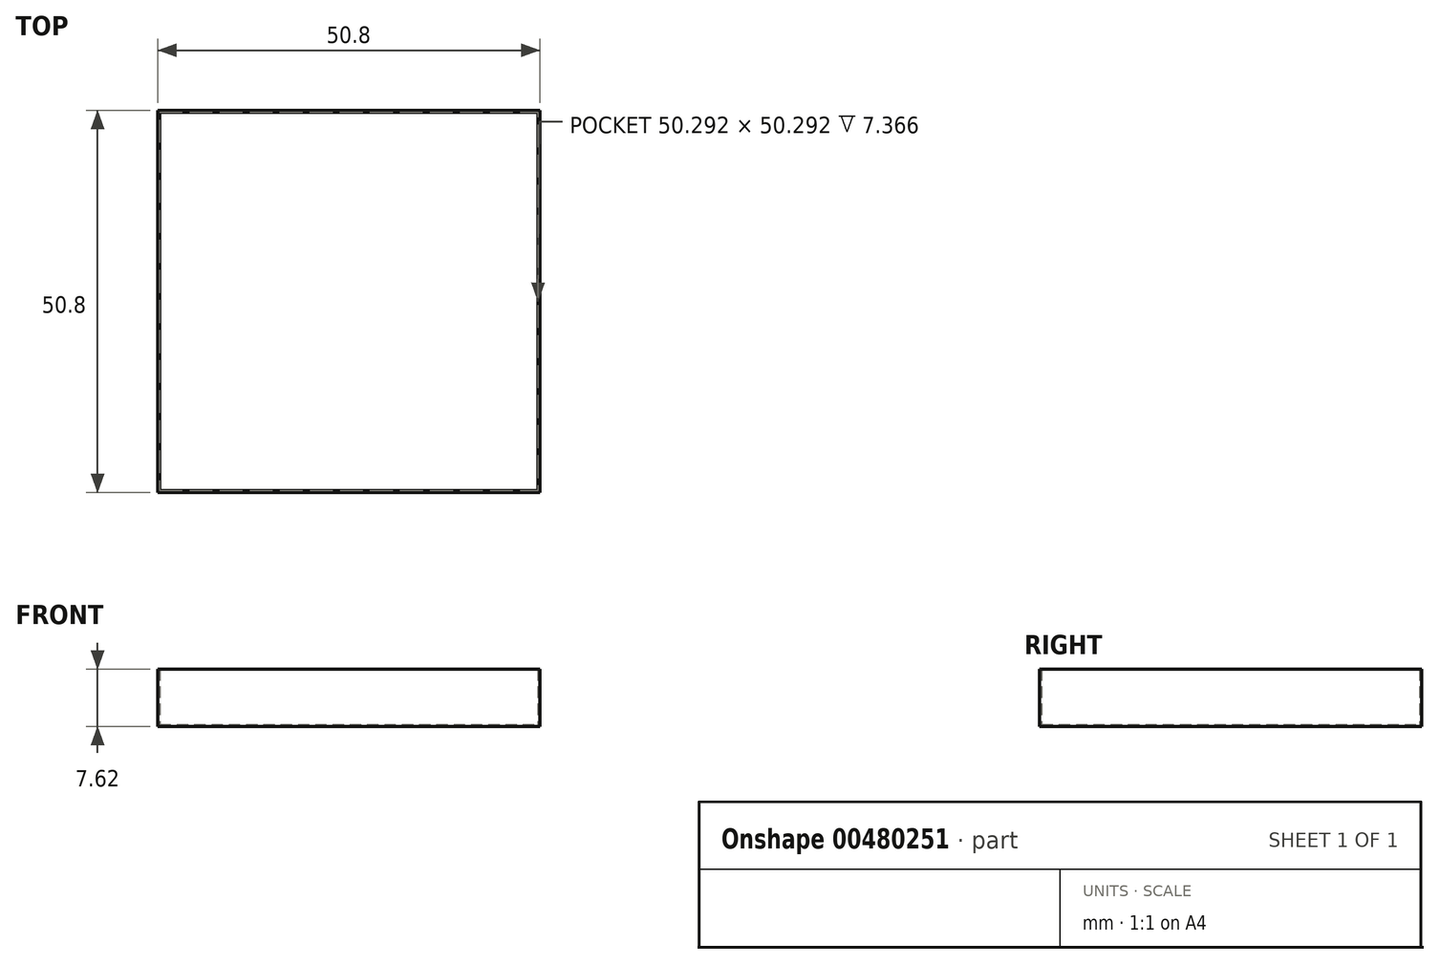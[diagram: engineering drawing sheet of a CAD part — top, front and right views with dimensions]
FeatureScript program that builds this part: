
annotation { "Feature Type Name" : "Feature", "Feature Type Description" : "" }
export const myFeature = defineFeature(function(context is Context, id is Id, definition is map)
    precondition{}
    {
        {
            var Q0;
            Q0=qCreatedBy(makeId("Top.planeOp"),FACE);
            var sketch = newSketch(context, id + "F0", { "sketchPlane" : qUnion([Q0])});
            skPoint(sketch, "E0.middle", {"position": v(0, 0) * mm});
            skPoint(sketch, "E0.right.start.orphan", {"position": v(-21.96, 12.13) * mm});
            skPoint(sketch, "E0.top.end.orphan", {"position": v(-21.96, -12.13) * mm});
            skPoint(sketch, "E0.left.end.orphan", {"position": v(21.96, -12.13) * mm});
            skPoint(sketch, "E0.left.start.orphan", {"position": v(21.96, 12.13) * mm});
            skLineSegment(sketch, "E1.bottom", {"start": v(0, 0) * mm, "end": v(50.8, 0) * mm});
            skLineSegment(sketch, "E1.top", {"start": v(0, 50.8) * mm, "end": v(50.8, 50.8) * mm});
            skLineSegment(sketch, "E1.left", {"start": v(0, 0) * mm, "end": v(0, 50.8) * mm});
            skLineSegment(sketch, "E1.right", {"start": v(50.8, 0) * mm, "end": v(50.8, 50.8) * mm});
            skPoint(sketch, "E2.firstSnap0", {"position": v(25.4, 0) * mm});
            skPoint(sketch, "E2.left.start.orphan", {"position": v(25.4, -18.03) * mm});
            skSolve(sketch);
        }
        {
            var Q0;
            Q0=makeQuery(id+"F0.imprint","IMPRINT",FACE,{"disambiguationData":[TD([[makeQuery(id+"F0.imprint","IMPRINT",EDGE,{"derivedFrom":sQuery(id+"F0.wireOp",EDGE,"E1.bottom")}),1.0]])]});
            extrude(context, id + "F1", {"entities" : qUnion([Q0]), "depth" : 7.62 * mm, "offsetDistance" : 25.4 * mm});
        }
        {
            var Q0;
            Q0=makeQuery(id+"F1.opExtrude","CAP_FACE",FACE,{"disambiguationData":[OSD([sQuery(id+"F0.wireOp",EDGE,"E1.bottom"),sQuery(id+"F0.wireOp",EDGE,"E1.top"),sQuery(id+"F0.wireOp",EDGE,"E1.left"),sQuery(id+"F0.wireOp",EDGE,"E1.right")])],"isStart":false});
            shell(context, id + "F2", {"entities" : qUnion([Q0]), "thickness" : 0.25 * mm});
        }
    });
